# Revit family: Sink-Vessel-Lavatory-KOHLER-FOREFRONT-K-2660T_1
name_source: partatom
category: Plumbing Fixtures
units: mm (PartAtom-declared; Revit-internal decimal feet)

## family parameters
Cut with Voids When Loaded = No
Host = Face
OmniClass Number = 23.31.13.00
OmniClass Title = Sinks
Part Type = Normal
Room Calculation Point = No
Round Connector Dimension = Use Diameter
Shared = No

## types (4) — shared parameters
ADA Compliant = No
Assembly Code = D2010400
CW Connection = No
Cold Water Inlet = Cold Water Inlet
Date Modified = 11/20/2023
Default Elevation = 36"
Drain Included = No
Flow Rate = 0 GPM
HW Connection = No
Height = 6 13/16"
Hot Water Inlet = Hot Water Inlet
Length = 23"
Manufacturer = Kohler Co.
Master Format 2014 = 22 41 16
Master Format 2014 Name = Residential Lavatories and Sinks
Material = Vitreous China
Pressure = 0.00 psi
Product Documentation Link = https://files.kohler.com.cn
Product Name = FOREFRONT
URL = http://www.kohler.com.cn
Vent Connection = No
Waste Connection = Yes
Waste Water Outlet = Waste Water Outlet
WaterSense Certified = No
Width = 18 1/8"

## per-type parameters (varying)
| type | 8 Inch Widespread Faucet Holes | Description | Faucet Hole Spacing | Finish | Model | Product Page URL | Single Faucet Hole | Type |
| Single Faucet Hole, 0-White | No | Rectangular fashionable washbasin with Single Faucet Hole | 0" | Kohler-Vitreous_China-0-White | K-2660T-1-0 | https://www.kohler.com.cn | Yes | 1 |
| 8 Inch Widespread Faucet Holes, 0-White | Yes | Rectangular fashion washbasin with 8 inch Faucet Hole | 8" | Kohler-Vitreous_China-0-White | K-2660T-8-0 | https://www.kohler.com.cn | No | 2 |
| Single Faucet Hole, 17-Teal | No | Rectangular fashionable washbasin with Single Faucet Hole | 0" | KOHLER-Vitreous_China-17-Teal | K-2660T-1-17 |  | Yes | 3 |
| Single Faucet Hole, 42-Aspen Green | No | Rectangular fashionable washbasin with Single Faucet Hole | 0" | KOHLER-Vitreous_China-42-Aspen_Green | K-2660T-1-42 |  | Yes | 4 |

## geometry (parser evidence)
native form markers: Sweep x6
no freeform markers — native parametric forms only
